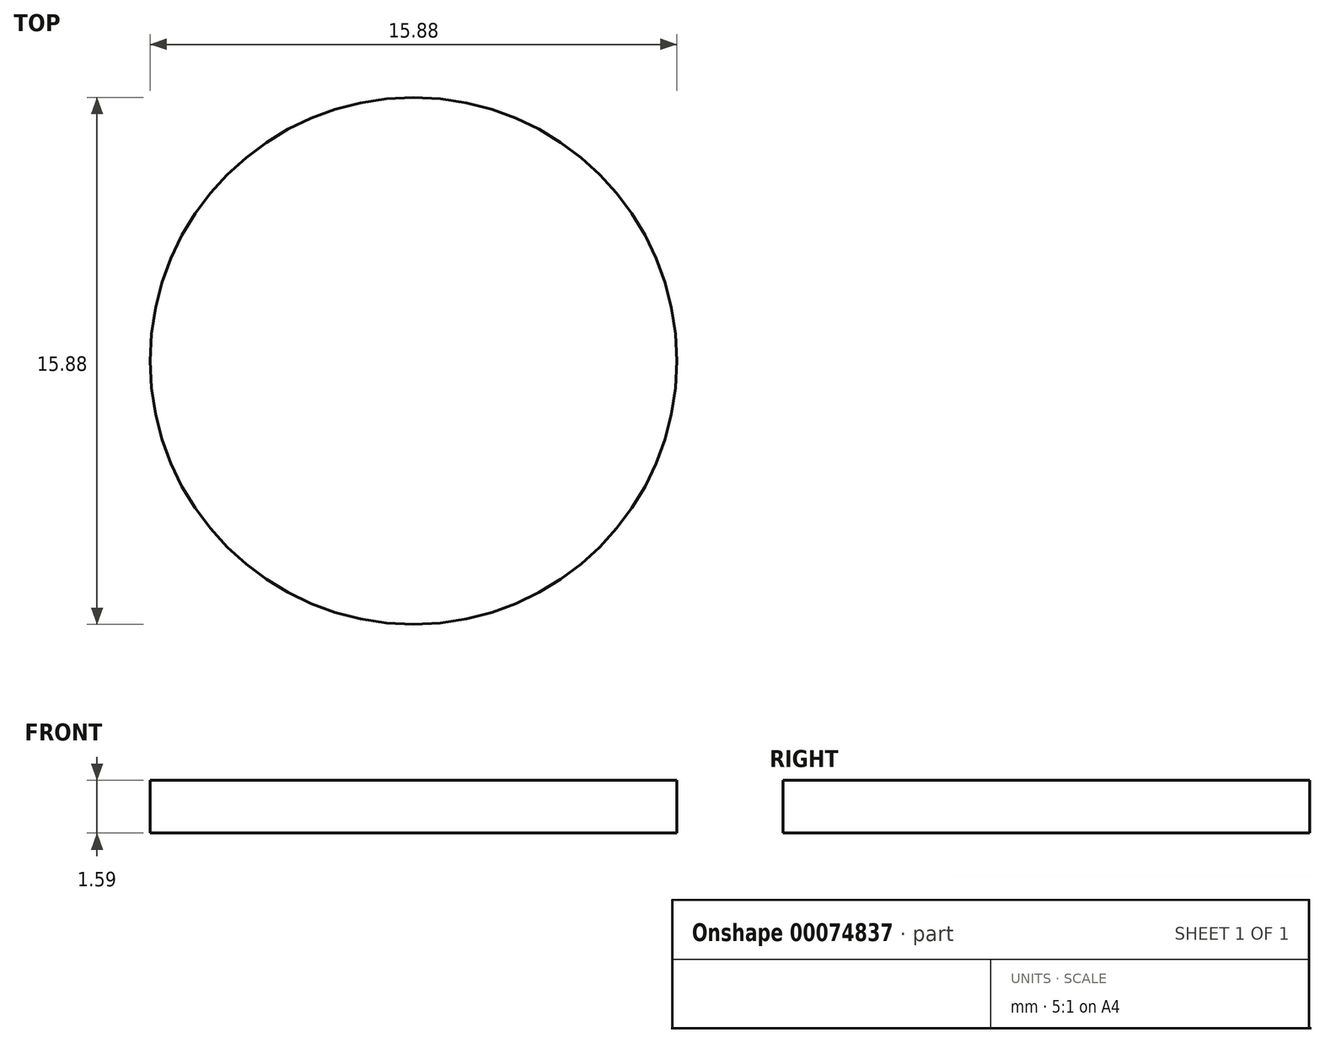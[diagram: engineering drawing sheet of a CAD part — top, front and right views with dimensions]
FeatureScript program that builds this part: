
annotation { "Feature Type Name" : "Feature", "Feature Type Description" : "" }
export const myFeature = defineFeature(function(context is Context, id is Id, definition is map)
    precondition{}
    {
        {
            var Q0;
            Q0=qCreatedBy(makeId("Top.planeOp"),FACE);
            var sketch = newSketch(context, id + "F0", { "sketchPlane" : qUnion([Q0])});
            skCircle(sketch, "E0", {"center": v(0, 0) * mm, "radius": 7.94 * mm});
            skSolve(sketch);
        }
        {
            var Q0;
            Q0=makeQuery(id+"F0.imprint","IMPRINT",FACE,{"disambiguationData":[TD([[makeQuery(id+"F0.imprint","IMPRINT",EDGE,{"derivedFrom":sQuery(id+"F0.wireOp",EDGE,"E0")}),1.0]])]});
            extrude(context, id + "F1", {"entities" : qUnion([Q0]), "depth" : 1.59 * mm});
        }
    });
